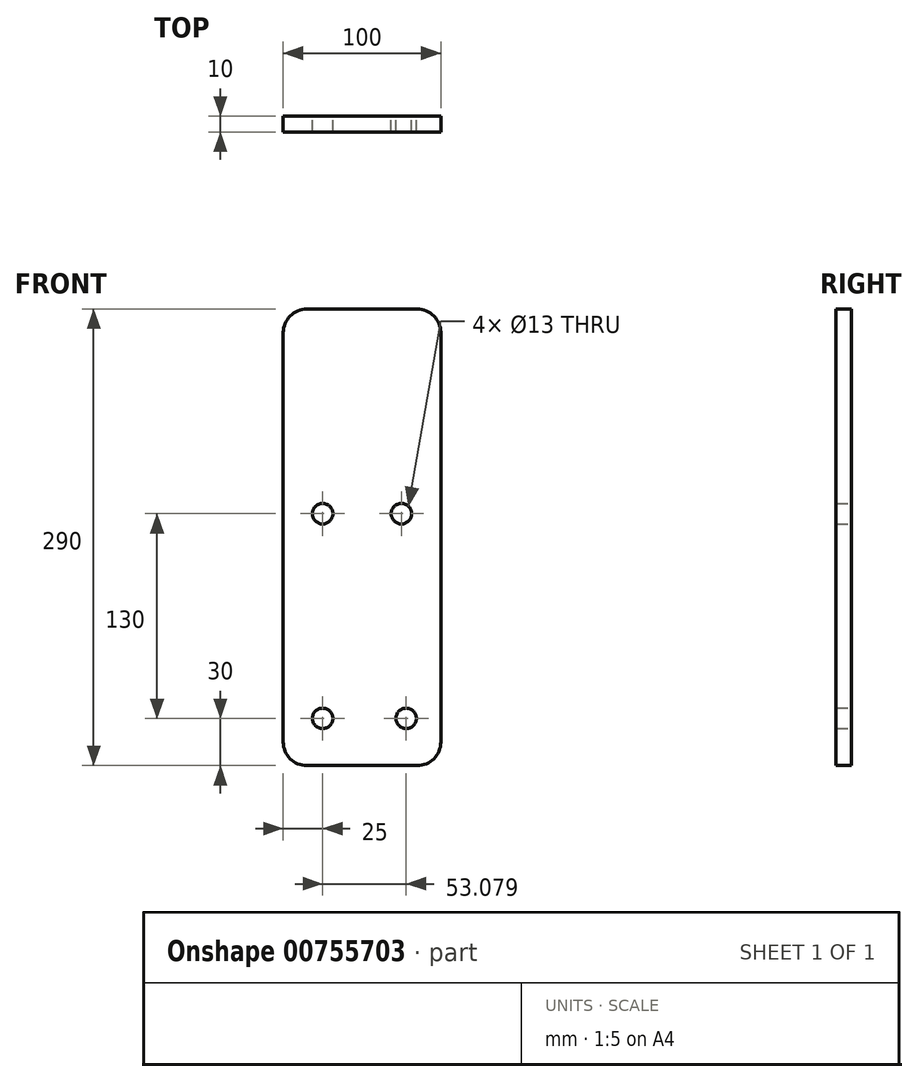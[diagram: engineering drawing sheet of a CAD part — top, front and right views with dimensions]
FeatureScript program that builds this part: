
annotation { "Feature Type Name" : "Feature", "Feature Type Description" : "" }
export const myFeature = defineFeature(function(context is Context, id is Id, definition is map)
    precondition{}
    {
        {
            var Q0;
            Q0=qCreatedBy(makeId("Front.planeOp"),FACE);
            var sketch = newSketch(context, id + "F0", { "sketchPlane" : qUnion([Q0])});
            skLineSegment(sketch, "E0.bottom", {"start": v(15, 0) * mm, "end": v(85, 0) * mm});
            skLineSegment(sketch, "E0.top", {"start": v(15, 290) * mm, "end": v(85, 290) * mm});
            skLineSegment(sketch, "E0.left", {"start": v(0, 15) * mm, "end": v(0, 275) * mm});
            skLineSegment(sketch, "E0.right", {"start": v(100, 15) * mm, "end": v(100, 275) * mm});
            skCircle(sketch, "E1", {"center": v(25, 160) * mm, "radius": 6.5 * mm});
            skCircle(sketch, "E2", {"center": v(75, 160) * mm, "radius": 6.5 * mm});
            skCircle(sketch, "E3", {"center": v(25, 30) * mm, "radius": 6.5 * mm});
            skCircle(sketch, "E4", {"center": v(78.08, 30) * mm, "radius": 6.5 * mm});
            skPoint(sketch, "E5.visualSharp", {"position": v(0, 290) * mm});
            skArc(sketch, "E5.filletArc", {"start": v(15, 290) * mm, "mid": v(4.4, 285.6) * mm, "end": v(0, 275) * mm});
            skPoint(sketch, "E6.visualSharp", {"position": v(100, 290) * mm});
            skArc(sketch, "E6.filletArc", {"start": v(100, 275) * mm, "mid": v(95.6, 285.6) * mm, "end": v(85, 290) * mm});
            skPoint(sketch, "E7.visualSharp", {"position": v(100, 0) * mm});
            skArc(sketch, "E7.filletArc", {"start": v(85, 0) * mm, "mid": v(95.6, 4.4) * mm, "end": v(100, 15) * mm});
            skPoint(sketch, "E8.visualSharp", {"position": v(0, 0) * mm});
            skArc(sketch, "E8.filletArc", {"start": v(0, 15) * mm, "mid": v(4.4, 4.4) * mm, "end": v(15, 0) * mm});
            skSolve(sketch);
        }
        {
            var Q0;
            Q0=makeQuery(id+"F0.imprint","IMPRINT",FACE,{"disambiguationData":[TD([[makeQuery(id+"F0.imprint","IMPRINT",EDGE,{"derivedFrom":sQuery(id+"F0.wireOp",EDGE,"E0.bottom")}),1.0]])]});
            extrude(context, id + "F1", {"entities" : qUnion([Q0]), "depth" : 10 * mm, "offsetDistance" : 25 * mm});
        }
    });
